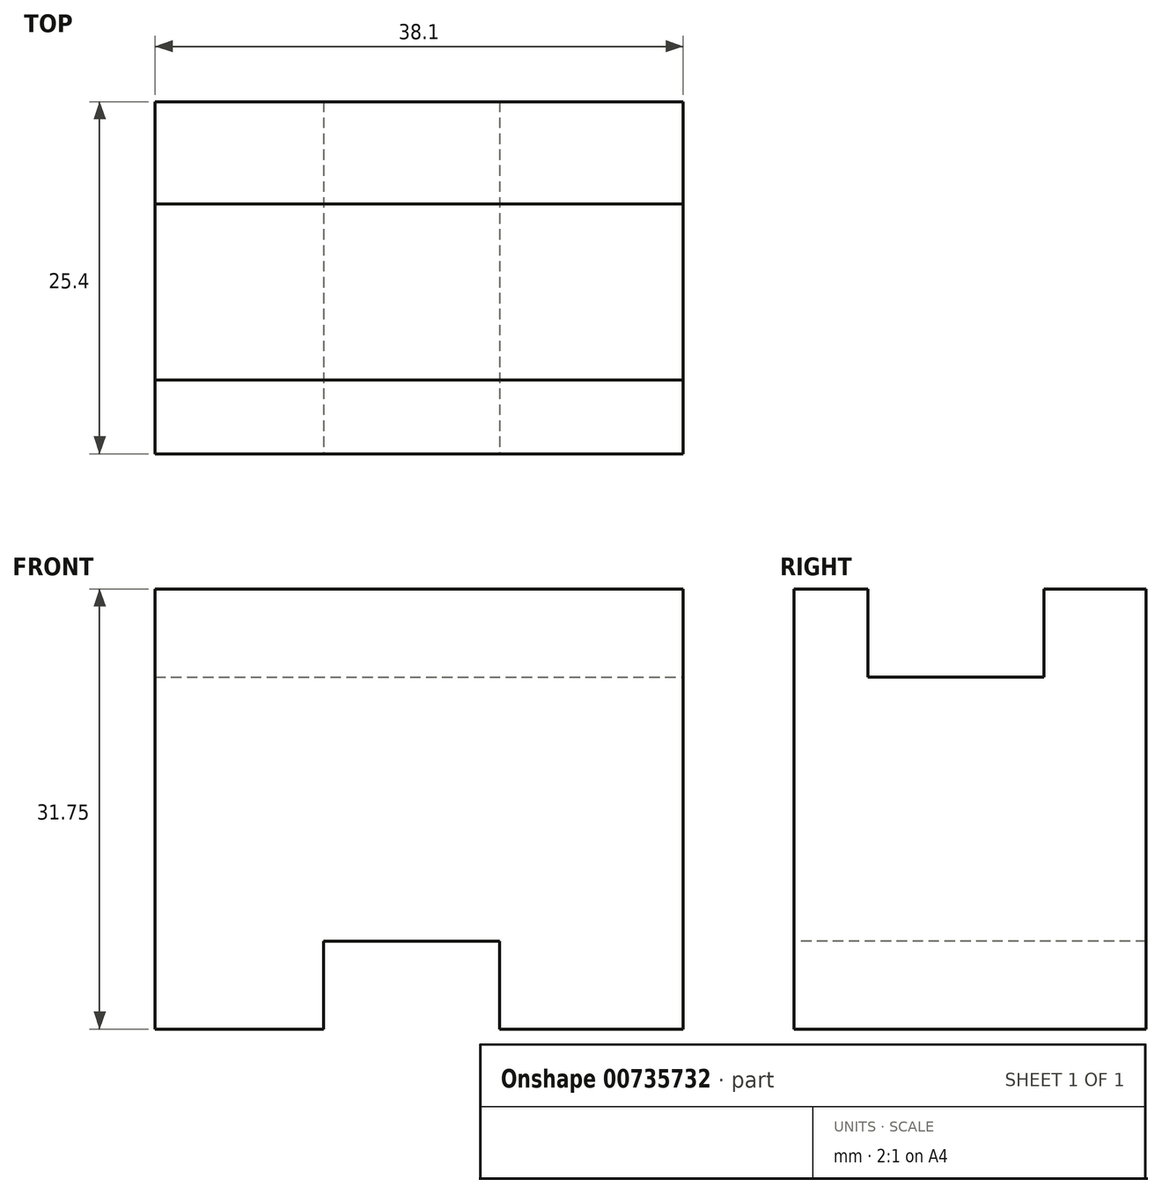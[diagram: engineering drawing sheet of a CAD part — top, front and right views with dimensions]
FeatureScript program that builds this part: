
annotation { "Feature Type Name" : "Feature", "Feature Type Description" : "" }
export const myFeature = defineFeature(function(context is Context, id is Id, definition is map)
    precondition{}
    {
        {
            var Q0;
            Q0=qCreatedBy(makeId("Right.planeOp"),FACE);
            var sketch = newSketch(context, id + "F0", { "sketchPlane" : qUnion([Q0])});
            skLineSegment(sketch, "E0", {"start": v(0, 0) * mm, "end": v(25.4, 0) * mm});
            skLineSegment(sketch, "E1", {"start": v(25.4, 0) * mm, "end": v(25.4, 31.75) * mm});
            skLineSegment(sketch, "E2", {"start": v(25.4, 31.75) * mm, "end": v(0, 31.75) * mm});
            skLineSegment(sketch, "E3", {"start": v(0, 31.75) * mm, "end": v(0, 0) * mm});
            skSolve(sketch);
        }
        {
            var Q0;
            Q0=makeQuery(id+"F0.imprint","IMPRINT",FACE,{"disambiguationData":[TD([[makeQuery(id+"F0.imprint","IMPRINT",EDGE,{"derivedFrom":sQuery(id+"F0.wireOp",EDGE,"E0")}),1.0]])]});
            extrude(context, id + "F1", {"entities" : qUnion([Q0]), "depth" : 38.1 * mm, "offsetDistance" : 25.4 * mm});
        }
        {
            var Q0;
            Q0=makeQuery(id+"F1.opExtrude","CAP_FACE",FACE,{"disambiguationData":[OSD([sQuery(id+"F0.wireOp",EDGE,"E0"),sQuery(id+"F0.wireOp",EDGE,"E1"),sQuery(id+"F0.wireOp",EDGE,"E2"),sQuery(id+"F0.wireOp",EDGE,"E3")])],"isStart":false});
            var sketch = newSketch(context, id + "F2", { "sketchPlane" : qUnion([Q0])});
            skLineSegment(sketch, "E4", {"start": v(5.33, 31.75) * mm, "end": v(5.33, 25.4) * mm});
            skLineSegment(sketch, "E5", {"start": v(5.33, 25.4) * mm, "end": v(18.03, 25.4) * mm});
            skLineSegment(sketch, "E6", {"start": v(18.03, 25.4) * mm, "end": v(18.03, 31.75) * mm});
            skSolve(sketch);
        }
        {
            var Q0;
            {var subQ0=sQuery(id+"F2.wireOp",EDGE,"E4");Q0=makeQuery(id+"F2.imprint","IMPRINT",FACE,{"disambiguationData":[TD([[makeQuery(id+"F2.imprint","IMPRINT",EDGE,{"derivedFrom":subQ0}),1.0]])]});}
            extrude(context, id + "F3", {"entities" : qUnion([Q0]), "operationType" : NewBodyOperationType.REMOVE, "oppositeDirection" : true, "depth" : 38.1 * mm, "offsetDistance" : 25.4 * mm});
        }
        {
            var Q0;
            Q0=makeQuery(id+"F1.opExtrude","SWEPT_FACE",FACE,{"disambiguationData":[OSD([sQuery(id+"F0.wireOp",EDGE,"E3")])]});
            var sketch = newSketch(context, id + "F4", { "sketchPlane" : qUnion([Q0])});
            skLineSegment(sketch, "E7", {"start": v(12.16, 0) * mm, "end": v(12.16, 6.35) * mm});
            skLineSegment(sketch, "E8", {"start": v(12.16, 6.35) * mm, "end": v(24.86, 6.35) * mm});
            skLineSegment(sketch, "E9", {"start": v(24.86, 6.35) * mm, "end": v(24.86, 0) * mm});
            skLineSegment(sketch, "E10", {"start": v(12.16, 0) * mm, "end": v(24.86, 0) * mm});
            skSolve(sketch);
        }
        {
            var Q0;
            Q0=makeQuery(id+"F4.imprint","IMPRINT",FACE,{"disambiguationData":[TD([[makeQuery(id+"F4.imprint","IMPRINT",EDGE,{"derivedFrom":sQuery(id+"F4.wireOp",EDGE,"E7")}),-1.0]])]});
            extrude(context, id + "F5", {"entities" : qUnion([Q0]), "operationType" : NewBodyOperationType.REMOVE, "oppositeDirection" : true, "depth" : 38.1 * mm, "offsetDistance" : 25.4 * mm});
        }
    });
